# Revit family: Cassettes MTP
name_source: partatom
category: Installations électriques
units: mm (PartAtom-declared; Revit-internal decimal feet)

## family parameters
Basée sur le plan de construction = Non
Conserver l'orientation des annotations = Non
Cote de connecteur circulaire = Utiliser le diamètre
Couper avec des vides une fois chargée = Non
Partagée = Non
Point de calcul de pièce = Non
Toujours verticalement = Oui
Type d'élément = Normal

## types (8) — shared parameters
Avec boîtier = Oui
Avec façade = Non
Avec pigtails = Non
Couleur = IDS_NOIR
Hauteur = 43.7 mm  [stored 0.143373 ft]
Largeur (mm) = 110 mm  [stored 0.360892 ft]
Lien e-catalogue = https://www.legrand.fr
Température de fonctionnement = -10°C à 60°C
Température de stockage = -10°C à 60°C
zero-valued in all types: Elévation par défaut

## per-type parameters (varying)
| type | Approprié pour nombre de connecteurs | Classe ETIM | Classe de fibre optique | Connecteurs LC | Connecteurs SC | Croisé | EAN | Fonction | Nombre de connecteurs face arrière | Nombre de connecteurs face avant | Profondeur | Référence Legrand | Type de connecteur externe | Type de connecteur interne | Type de fibre optique | Visibilité connecteurs LC | Visibilité connecteurs SC | Visibilité des connecteurs |
| Cassette MTP 24 LC OM4 panneau HD Ultra | 24 | EC001130 | OM4 | Connecteurs LC : 24 fibres OM4 multi mode | Connecteurs SC : 12 fibres OM4 multimode | Non | 3414970962140 | Cassettes Slim haute densité MTP | 2 | 24 | 196 mm  [stored 0.643045 ft] | 032142 | LC_DUPLEX | MT/MPO | Multimode | Oui | Non | Oui |
| Cassette MTP 12 SC OM4 panneau HD Ultra | 12 | EC001130 | OM4 | Connecteurs LC : 12 fibres OM4 multimode | Connecteurs SC : 12 fibres OM4 multimode | Oui | 3414970962164 | Cassettes Slim haute densité MTP | 1 | 12 | 196 mm  [stored 0.643045 ft] | 032143 | SC_DUPLEX | MT/MPO | Multimode | Non | Oui | Non |
| Cassette MTP 24 LC OS2 panneau HD Ultra | 24 | EC001130 | OS2 | Connecteurs LC : 24 fibres OS2 monomode | Connecteurs SC : 12 fibres OM4 multimode | Non | 3414970962188 | Cassettes Slim haute densité MTP | 2 | 24 | 196 mm  [stored 0.643045 ft] | 032144 | LC_DUPLEX | MT/MPO | Monomode | Oui | Non | Oui |
| Cassette MTP 12 SC OS2 panneau HD Ultra | 12 | EC001130 | OS2 | Connecteurs LC : 12 fibres OM4 multimode | Connecteurs SC : 12 fibres OS2 monomode | Oui | 3414970962201 | Cassettes Slim haute densité MTP | 1 | 12 | 196 mm  [stored 0.643045 ft] | 032145 | SC_DUPLEX | MT/MPO | Monomode | Non | Oui | Non |
| Cassette MTP 12 LC OM4 panneau HD Ultra | 12 | EC002699 | OM4 | Connecteurs LC : 12 fibres OM4 multimode | Connecteurs SC : 12 fibres OM4 multimode | Non | 3414971420236 | Cassettes haute densité MTP | 1 | 12 | 200 mm  [stored 0.656168 ft] | 032148 | LC_DUPLEX | MTP-M | Multimode | Oui | Non | Non |
| Cassette MTP 12 LC OS2 panneau HD Ultra | 12 | EC002699 | OS2 | Connecteurs LC : 12 fibres OS2 monomode | Connecteurs SC : 12 fibres OM4 multimode | Non | 3414971420250 | Cassettes haute densité MTP | 1 | 12 | 200 mm  [stored 0.656168 ft] | 032149 | LC_DUPLEX | MTP-M | Monomode | Oui | Non | Non |
| Cassette MTP 12 SC OM4 panneau HDÉ_UNIVERSELLE_ULTRA | 12 | EC002699 | OM4 | Connecteurs LC : 12 fibres OM4 multimode | Connecteurs SC : 12 fibres OM4 multimode | Oui | 3414971929296 | Cassettes haute densité MTP | 1 | 12 | 200 mm  [stored 0.656168 ft] | 032159 | SC_DUPLEX | MTP-M | Multimode | Non | Oui | Non |
| Cassette 12 SC MTP OS2 polarité universelle Ultra | 12 | EC002699 | OS2 | Connecteurs LC : 12 fibres OM4 multimode | Connecteurs SC : 12 fibres OS2 monomode | Oui | 3414971929319 | Cassettes haute densité MTP | 1 | 12 | 200 mm  [stored 0.656168 ft] | 032160 | SC_DUPLEX | MTP-M | Monomode | Non | Oui | Non |

note: column(s) folded — value = type name in every type: Libellé BIM

note: [stored X ft] marks values corroborated as IEEE doubles in the binary element streams (Revit-internal decimal feet)
